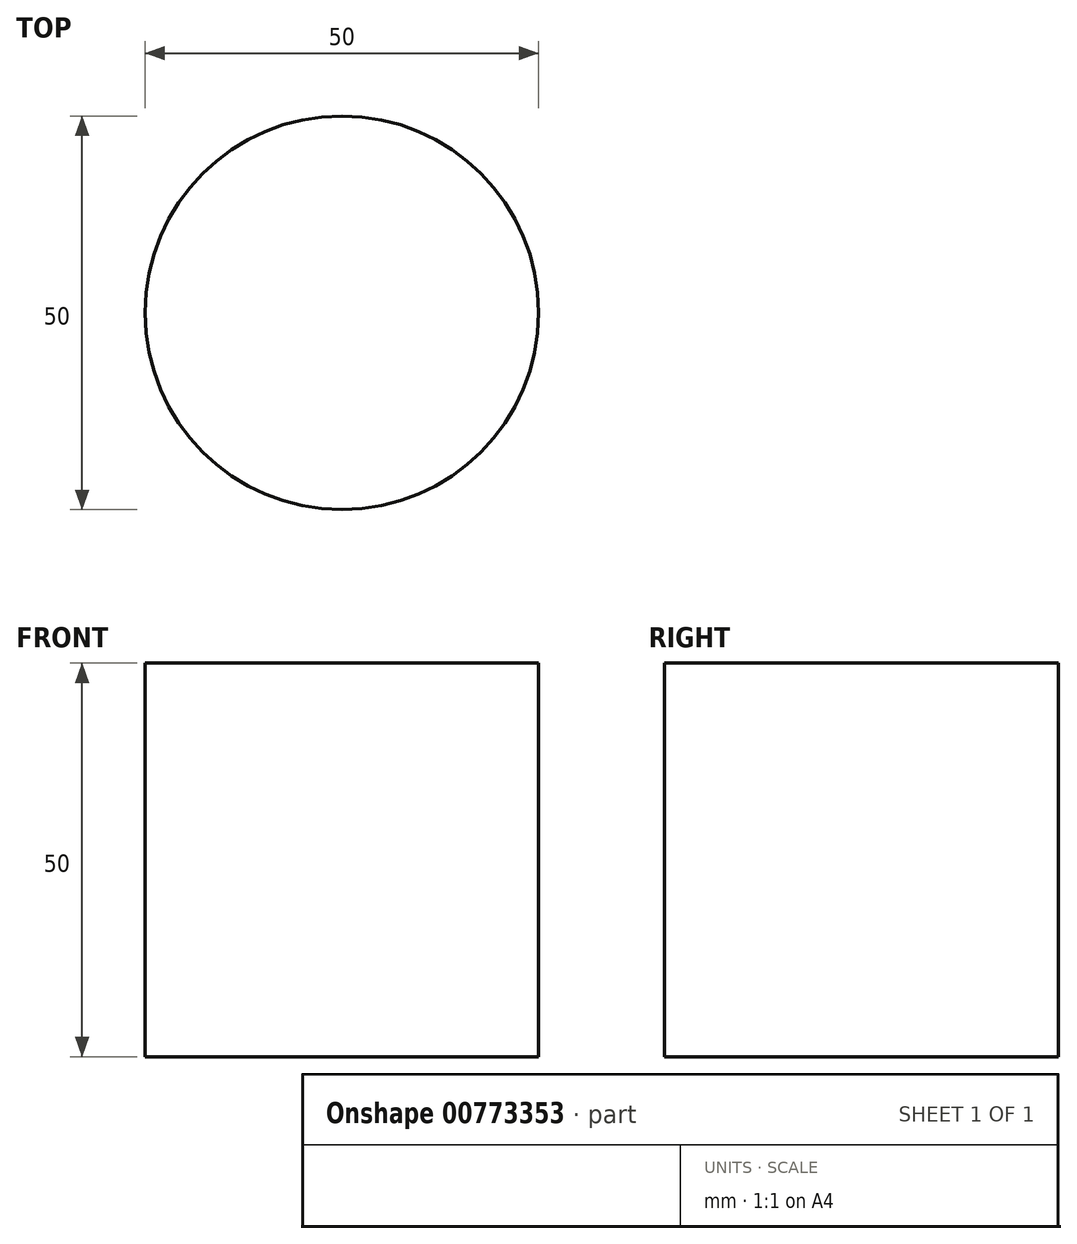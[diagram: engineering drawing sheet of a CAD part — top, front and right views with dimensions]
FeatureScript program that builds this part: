
annotation { "Feature Type Name" : "Feature", "Feature Type Description" : "" }
export const myFeature = defineFeature(function(context is Context, id is Id, definition is map)
    precondition{}
    {
        {
            var Q0;
            Q0=qCreatedBy(makeId("Top.planeOp"),FACE);
            var sketch = newSketch(context, id + "F0", { "sketchPlane" : qUnion([Q0])});
            skCircle(sketch, "E0", {"center": v(1.17, 0) * mm, "radius": 25 * mm});
            skSolve(sketch);
        }
        {
            var Q0;
            Q0=makeQuery(id+"F0.imprint","IMPRINT",FACE,{"disambiguationData":[TD([[makeQuery(id+"F0.imprint","IMPRINT",EDGE,{"derivedFrom":sQuery(id+"F0.wireOp",EDGE,"E0")}),1.0]])]});
            extrude(context, id + "F1", {"entities" : qUnion([Q0]), "depth" : 50 * mm, "offsetDistance" : 25 * mm});
        }
    });
